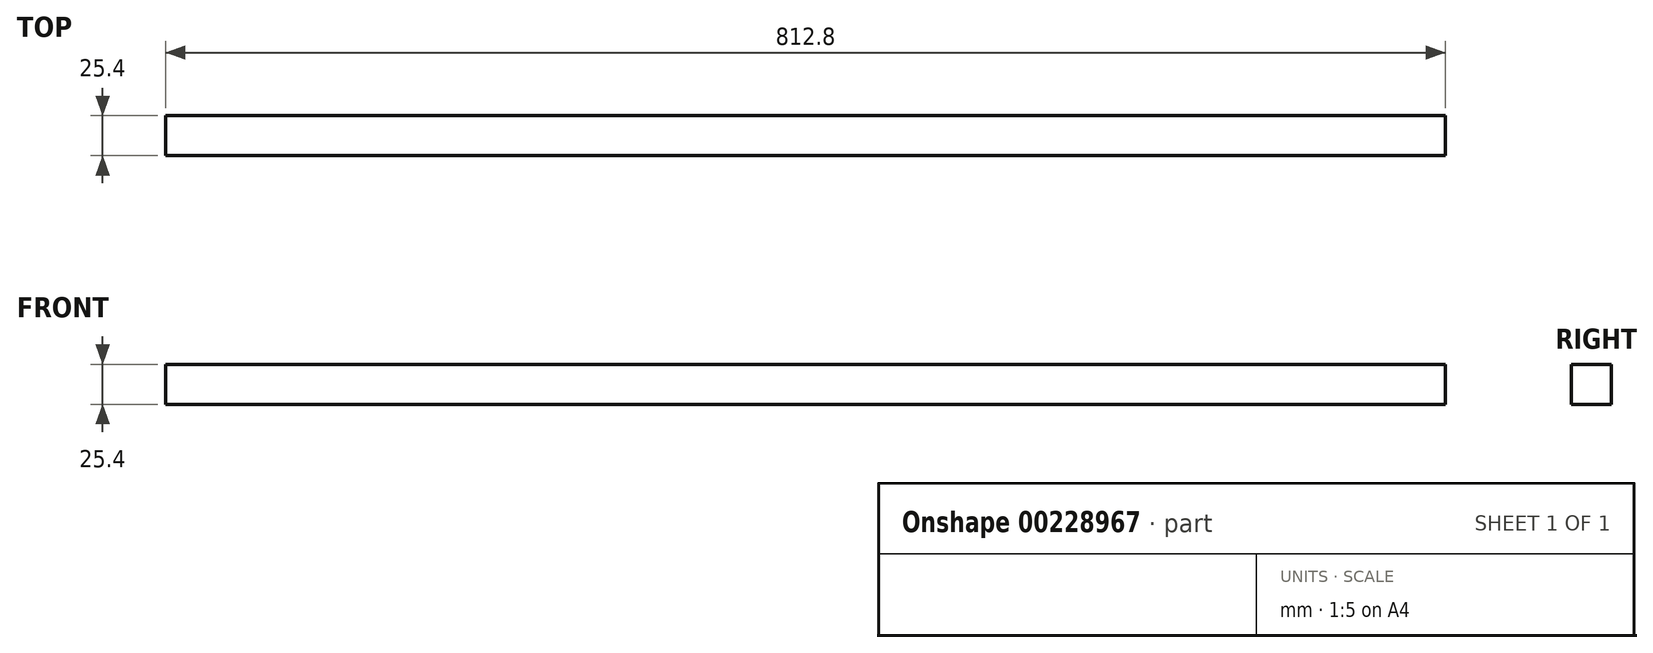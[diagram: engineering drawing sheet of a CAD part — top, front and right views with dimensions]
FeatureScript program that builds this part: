
annotation { "Feature Type Name" : "Feature", "Feature Type Description" : "" }
export const myFeature = defineFeature(function(context is Context, id is Id, definition is map)
    precondition{}
    {
        {
            var Q0;
            Q0=qCreatedBy(makeId("Top.planeOp"),FACE);
            var sketch = newSketch(context, id + "F0", { "sketchPlane" : qUnion([Q0])});
            skLineSegment(sketch, "E0.bottom", {"start": v(0, 0) * mm, "end": v(812.8, 0) * mm});
            skLineSegment(sketch, "E0.top", {"start": v(0, 25.4) * mm, "end": v(812.8, 25.4) * mm});
            skLineSegment(sketch, "E0.left", {"start": v(0, 0) * mm, "end": v(0, 25.4) * mm});
            skLineSegment(sketch, "E0.right", {"start": v(812.8, 0) * mm, "end": v(812.8, 25.4) * mm});
            skSolve(sketch);
        }
        {
            var Q0;
            Q0 = qSketchRegion(id + "F0", true);
            extrude(context, id + "F1", {"entities" : qUnion([Q0]), "depth" : 25.4 * mm});
        }
    });
